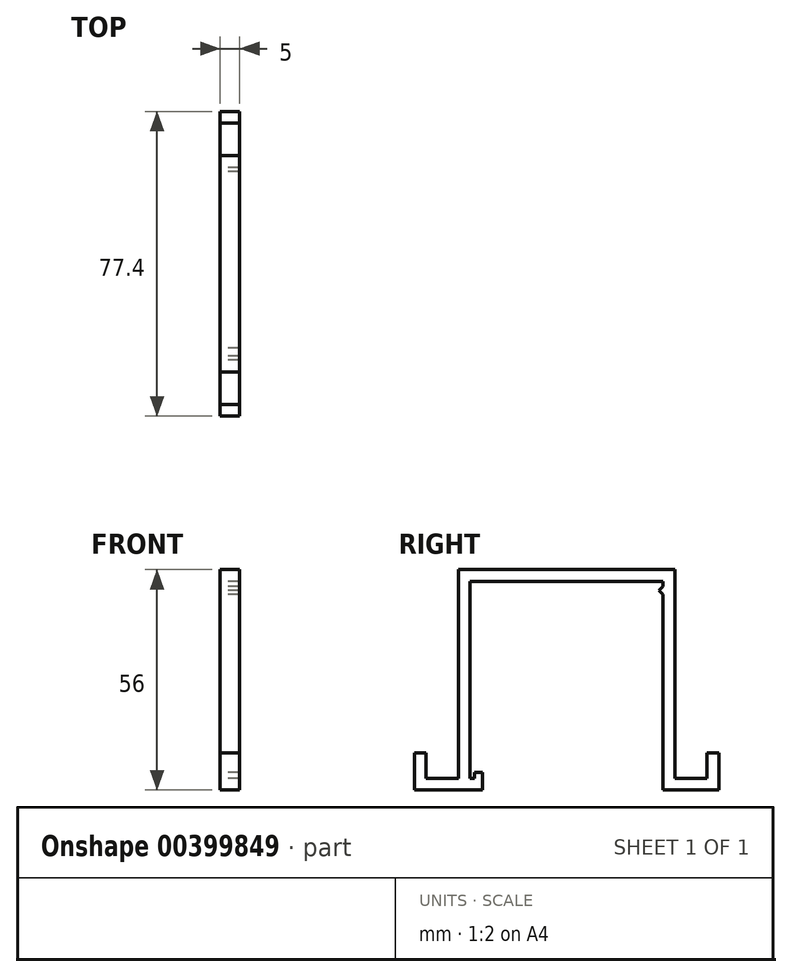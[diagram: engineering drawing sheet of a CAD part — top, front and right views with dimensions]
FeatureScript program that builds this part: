
annotation { "Feature Type Name" : "Feature", "Feature Type Description" : "" }
export const myFeature = defineFeature(function(context is Context, id is Id, definition is map)
    precondition{}
    {
        {
            var Q0;
            Q0=qCreatedBy(makeId("Right.planeOp"),FACE);
            var sketch = newSketch(context, id + "F0", { "sketchPlane" : qUnion([Q0])});
            skLineSegment(sketch, "E0", {"start": v(0, 50) * mm, "end": v(-24.5, 50) * mm});
            skLineSegment(sketch, "E1", {"start": v(-24.5, 50) * mm, "end": v(-24.5, 0) * mm});
            skLineSegment(sketch, "E2", {"start": v(-24.5, -3) * mm, "end": v(-38.7, -3) * mm});
            skLineSegment(sketch, "E3", {"start": v(-38.7, -3) * mm, "end": v(-38.7, 6.4) * mm});
            skLineSegment(sketch, "E4", {"start": v(-38.7, 6.4) * mm, "end": v(-35.7, 6.4) * mm});
            skLineSegment(sketch, "E5", {"start": v(-35.7, 6.4) * mm, "end": v(-35.7, 0) * mm});
            skLineSegment(sketch, "E6", {"start": v(-35.7, 0) * mm, "end": v(-27.5, 0) * mm});
            skLineSegment(sketch, "E7", {"start": v(-27.5, 0) * mm, "end": v(-27.5, 53) * mm});
            skLineSegment(sketch, "E8", {"start": v(-27.5, 53) * mm, "end": v(0, 53) * mm});
            skLineSegment(sketch, "E9", {"start": v(-24.5, 0) * mm, "end": v(-23.4, 0) * mm});
            skLineSegment(sketch, "E10", {"start": v(-23.4, 0) * mm, "end": v(-23.4, 1.5) * mm});
            skLineSegment(sketch, "E11", {"start": v(-23.4, 1.5) * mm, "end": v(-21.4, 1.5) * mm});
            skLineSegment(sketch, "E12", {"start": v(-21.4, 1.5) * mm, "end": v(-21.4, -2.97) * mm});
            skLineSegment(sketch, "E13", {"start": v(-21.4, -2.97) * mm, "end": v(-24.5, -3) * mm});
            skLineSegment(sketch, "E14.MirrorCS", {"start": v(38.7, -3) * mm, "end": v(38.7, 6.4) * mm});
            skLineSegment(sketch, "E15.MirrorCS", {"start": v(38.7, 6.4) * mm, "end": v(35.7, 6.4) * mm});
            skLineSegment(sketch, "E16.MirrorCS", {"start": v(35.7, 6.4) * mm, "end": v(35.7, 0) * mm});
            skLineSegment(sketch, "E17.MirrorCS", {"start": v(35.7, 0) * mm, "end": v(27.5, 0) * mm});
            skLineSegment(sketch, "E18.MirrorCS", {"start": v(24.5, -3) * mm, "end": v(38.7, -3) * mm});
            skLineSegment(sketch, "E19.MirrorCS", {"start": v(24.5, 50) * mm, "end": v(24.5, 48.7) * mm});
            skLineSegment(sketch, "E20.MirrorCS", {"start": v(27.5, 0) * mm, "end": v(27.5, 53) * mm});
            skLineSegment(sketch, "E21.MirrorCS", {"start": v(27.5, 53) * mm, "end": v(0, 53) * mm});
            skLineSegment(sketch, "E22.MirrorCS", {"start": v(0, 50) * mm, "end": v(24.5, 50) * mm});
            skLineSegment(sketch, "E23", {"start": v(24.5, 0) * mm, "end": v(24.5, -3) * mm});
            skLineSegment(sketch, "E24", {"start": v(24.5, 48.7) * mm, "end": v(23.5, 47.66) * mm});
            skLineSegment(sketch, "E25", {"start": v(23.5, 47.66) * mm, "end": v(24.5, 46.7) * mm});
            skLineSegment(sketch, "E26.trimOffspring", {"start": v(24.5, 46.7) * mm, "end": v(24.5, 0) * mm});
            skSolve(sketch);
        }
        {
            var Q0;
            Q0=makeQuery(id+"F0.imprint","IMPRINT",FACE,{"disambiguationData":[TD([[makeQuery(id+"F0.imprint","IMPRINT",EDGE,{"derivedFrom":sQuery(id+"F0.wireOp",EDGE,"E0")}),-1.0]])]});
            extrude(context, id + "F1", {"entities" : qUnion([Q0]), "depth" : 5 * mm});
        }
    });
